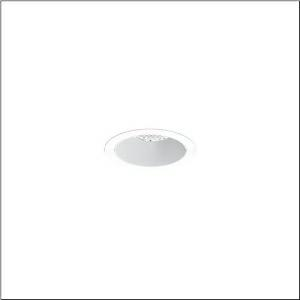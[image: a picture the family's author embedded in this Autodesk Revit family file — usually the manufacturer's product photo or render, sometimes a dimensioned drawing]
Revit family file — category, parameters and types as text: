
# Revit family: lunis_21_m_51db18mc91c
name_source: partatom
category: Lighting Fixtures
units: mm (PartAtom-declared; Revit-internal decimal feet)

## family parameters
Cut with Voids When Loaded = No
Host = Face
Light Source = No
Part Type = Normal
Room Calculation Point = No
Round Connector Dimension = Use Diameter
Shared = No

## types (1)
- --- (1 x LED, 4000 lm, 25.5 W, 6500K)
    Apparent Load = 26 VA
    CIE Flux Codes = 86 95 99 100 100
    Color Rendering = 80
    Color Temperature = 6500K
    Default Elevation = 1800 mm
    Description = Lunis 21,  M, downlight, light control with lens, of PMMA, anti glare with reflector, of PC, light emission: direct distribution, LED rated luminous flux: 1.840lm, light colour: 830/840/865, with terminal, 3-pole, mains connection: 220..240V, AC/DC, 0/50..60Hz, housing, round, of diecast aluminium, traffic white (RAL 9016), diameter: 115mm, clamping range: 1..40mm, protection rating (complete): IP20, protection rating (on room side): IP54, insulation class (complete): insulation class II (safety insulation), certification: CE, impact resistance: IK03, packaging unit: 1 piece
    Height = 0 mm  [stored 0 ft]
    Lamp = 1 x LED
    Lamp Light Flux = 4000 lm
    Lamp Power = 25.5 W
    Lamp count = 1
    Length = 115 mm
    Luminous efficacy = 157 lm/W
    Manufacturer = Siteco
    ModVariant = No
    Model = 51DB18MC91C
    Mounting Place = Ceiling
    Mounting Type = Recessed
    Number of Poles = 1
    OnlyDefault = Yes
    Power Factor = 1
    Product Name = Lunis 21 M
    Product group = downlight
    ProductGroupID = 400
    Protection Class = Protection class II
    Protection Degree = IP 20
    RLX_Detail_Level = 1
    RLX_Emergency_Light_Flux = 0 lm
    RLX_Emergency_Type = 0
    RLX_Emergency_Type_DB = No
    RlxData = <blob elided: 14077 chars, md5=9feb17d0>
    Socket = socket
    Standby Power = 0 W
    System Light Flux = 4000 lm
    System Power = 26 W
    Type Comments = individual setting: colour temperature 6500K, luminous flux: 100 % | (ON | ON | OFF | OFF) | 700 mA
    Type Image = l_1290852.jpg
    URL = http://relux.com
    VarID = @adj_019616
    Voltage = 0 V
    Weight = 0.00 kg
    Width = 0 mm  [stored 0 ft]

note: [stored X ft] marks values corroborated as IEEE doubles in the binary element streams (Revit-internal decimal feet)

## geometry (parser evidence)
native form markers: Sweep x10
no freeform markers — native parametric forms only
